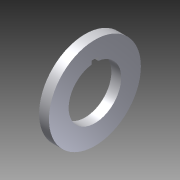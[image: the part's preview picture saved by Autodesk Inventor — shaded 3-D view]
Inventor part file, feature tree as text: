
AUTODESK INVENTOR PART (.ipt)
format: ipt  version: 2012 (Build 160160000, 160)  size: 602,112 bytes
history: native  units: in
note: dims shown in document units (in); Inventor stores cm internally (conversion verified against a paired STEP export)
features: extrude x2, sketch x1, imported_body x1
ambient origin geometry x8: Origin, YZ Plane, XZ Plane, XY Plane, X Axis, Y Axis, Z Axis, Center Point
feature tree (4):
  sketch  "Sketch1"  dims[d0=0.375in d3=0.3in d4=0.0in d5=1.0in d6=0.125in d7=0.125in d8=0.0625in d9=0.5625in d10=1.75in d11=1.0in d12=0.0in]
  extrude  "Extrusion2"  Depth=0.3in TaperAngle=0.0deg
  extrude  "Extrusion3"  Depth=1.0in
  imported_body  "Base1"
